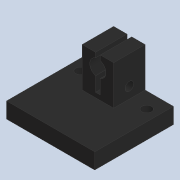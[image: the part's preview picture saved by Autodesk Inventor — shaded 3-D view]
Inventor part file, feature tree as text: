
AUTODESK INVENTOR PART (.ipt)
format: ipt  version: 2020 (Build 240168000, 168)  size: 173,056 bytes
history: native  units: mm
features: sketch x5, extrude x4, other x3, reference x2, hole x1, projected_geometry x1
ambient origin geometry x8: Origin, YZ Plane, XZ Plane, XY Plane, X Axis, Y Axis, Z Axis, Center Point
bodies: Solid1 (feature_tree)
feature tree (16):
  extrude  "Extrusion1"  Depth=20.0mm
  hole  "Hole1"  [1 undecoded]
  extrude  "Extrusion3"  Depth=3.0mm
  extrude  "Extrusion2"  Depth=18.0mm
  extrude  "Extrusion4"  Depth=10.0mm
  sketch  "Sketch1"  dims[d0=10.0mm d1=20.0mm]
  sketch  "Sketch2"  dims[d2=10.3mm d3=17.0mm]
  sketch  "Sketch3"  dims[d4=8.0mm d5=3.0mm]
  sketch  "Sketch4"  dims[d6=14.0mm d7=18.0mm]
  projected_geometry  "Projected Loop1"
  sketch  "Sketch5"  dims[d8=20.0mm d9=0.0mm d10=6.0mm d11=6.0mm d12=11.0mm d13=2.0mm d14=90.0deg d15=8.0mm d16=20.594885mm d18=5.5mm d19=8.0mm d21=8.0mm d22=13.0mm d23=0.0mm d25=30.0mm d26=0.0mm d27=10.0mm d28=0.0mm d29=7.0mm d30=7.0mm d31=5.0mm]
  reference  "Reference1"
  reference  "Reference2"
  parser-record x1  (decoder bookkeeping rows leaked as tree rows — omitted from the tree; the rows remain in map.json)
  other  "0008-10-03 YAxis.iam"
  other  "0008-20-1003 Switch.ipt:25"
note: 1 required parameter value undecoded (feature->parameter linkage not recoverable at this tier; creation-order binding heuristic only, values carry confidence <= 0.55)
note: 1 file-system path scrubbed to <path> (originals preserved in map.json)
